# Revit family: Water_Heater-Rinnai-Hybrid_Tank-Tankless-RH180
name_source: partatom
category: Mechanical Equipment
revit_build: Autodesk Revit MEP 2012 (Build: 20110916_2132(x64)
units: mm (PartAtom-declared; Revit-internal decimal feet)

## types (1)
- Standard
    04 CSI = 22 34 13
    95 CSI = 15480
    Applicable Altitude Range = 0 - 5400 ft (0 - 1646 m)
    Assembly Code = D3010500
    Cold Water Connector = Cold Water Connection
    Cold Water Outlet Radius = 3/4"
    Combustion Air = Indoor
    Condensate Drain Outlet = Condensate Drain Outlet Connection
    Depth = 27 1/2"
    Description = Hybrid Tank-Tankless Water Heater
    Dry Weight = 414.00 lb
    Electrical Consumption Range = Normal: 64 w, Standby: 2 w
    Exhaust Vent Length Note = 100 ft
    Frequency = 60 Hz
    Gas Input Range = 59,500-91,300 BTU/h (NG); 47,600-87,300 BTU/h (Propane)
    Gas Input Rate = 91.3 Btu/h
    Height = 51 51/256"
    Hot Water Connector = Hot Water Connection
    Hot Water Outlet Radius = 3/4"
    Installation Location = Indoor and outdoor
    Installation URL = https://www.rinnai.us
    Manufacturer = Rinnai America Corporation
    Manufacturer Fax = 678-829-1666
    Max Amperage = 8 A
    Model = REU-VA1320WF-US
    Product Page URL = http://www.rinnai.us
    Recovery for 100 Deg Rise = 528-668 gal/h
    Spec Sheet URL = http://www.rinnai.us
    Storage Tank Volume = 100 gal/min
    Storage Tank Volume Note = 100-300 gal
    Subcategory = Tankless Water Heaters
    Thermal Efficiency Rating = 0.96
    URL = http://www.rinnai.us
    Unit = Metal - Rinnai - Aluminum Frame - Painted White
    Unit Top = Metal - Rinnai - Stainless Steel
    Vent Connector = Vent Connection
    Venting = 4" UL listing type B-vent
    Voltage = 120 V
    Warranty URL = http://www.rinnai.us
    Wattage = 64 W
    Width = 20"
    ecoScorecard Product Page = http://products.ecoscorecard.com
    ecoScorecard_data = http://products.ecoscorecard.com

## geometry (parser evidence)
native form markers: Blend x4, Sweep x4
no freeform markers — native parametric forms only
